# Revit family: 903-20-001-DN65-400
name_source: partatom
category: Pipe Accessories
units: mm (PartAtom-declared; Revit-internal decimal feet)

## family parameters
Always vertical = Yes
Cut with Voids When Loaded = No
Part Type = Valve - Breaks Into
Round Connector Dimension = Use Diameter
Shared = No
Work Plane-Based = No

## types (15) — shared parameters
903-065-20-11000 = DN65_PN16
903-080-20-11000 = DN80_PN16
903-100-20-11000 = DN100_PN16
903-125-20-11000 = DN125_PN16
903-150-20-11000 = DN150_PN16
903-200-20-01000 = DN200_PN10
903-200-20-11000 = DN200_PN16
903-250-20-01000 = DN250_PN10
903-250-20-11000 = DN250_PN16
903-300-20-01000 = DN300_PN10
903-300-20-11000 = DN300_PN16
903-350-20-01000 = DN350_PN10
903-350-20-11000 = DN350_PN16
903-400-20-01000 = DN400_PN10
903-400-20-11000 = DN400_PN16
Description_ = AVK SILENT CHECK VALVE
Search_table = 903-20-001-DN65-400
URL product pages = https://www.avkvalves.com

## per-type parameters (varying)
| type | Bodywall_thickness | D2 | DN | Flange_thickness | Flange_thickness_2 | Flange_thickness_3 | ID | L | L_ref | L_ref_2 | W |
| DN065_PN16 | 43 mm | 59 mm | 65 mm  [stored 0.213255 ft] | 10 mm  [stored 0.0328084 ft] | 5 mm  [stored 0.0164042 ft] | 15 mm  [stored 0.0492126 ft] | 33 mm | 140 mm  [stored 0.459318 ft] | 20 mm  [stored 0.0656168 ft] | 15 mm  [stored 0.0492126 ft] | 93 mm |
| DN080_PN16 | 50 mm  [stored 0.164042 ft] | 66 mm  [stored 0.216535 ft] | 80 mm  [stored 0.262467 ft] | 10 mm  [stored 0.0328084 ft] | 5 mm  [stored 0.0164042 ft] | 15 mm  [stored 0.0492126 ft] | 40 mm  [stored 0.131234 ft] | 152 mm  [stored 0.498688 ft] | 15 mm  [stored 0.0492126 ft] | 20 mm  [stored 0.0656168 ft] | 100 mm  [stored 0.328084 ft] |
| DN100_PN16 | 60 mm  [stored 0.19685 ft] | 78 mm  [stored 0.255906 ft] | 100 mm  [stored 0.328084 ft] | 10 mm  [stored 0.0328084 ft] | 5 mm  [stored 0.0164042 ft] | 15 mm  [stored 0.0492126 ft] | 50 mm  [stored 0.164042 ft] | 184 mm  [stored 0.603675 ft] | 20 mm  [stored 0.0656168 ft] | 20 mm  [stored 0.0656168 ft] | 118 mm  [stored 0.387139 ft] |
| DN125_PN16 | 73 mm | 92 mm  [stored 0.301837 ft] | 125 mm  [stored 0.410105 ft] | 10 mm  [stored 0.0328084 ft] | 5 mm  [stored 0.0164042 ft] | 15 mm  [stored 0.0492126 ft] | 63 mm | 216 mm | 20 mm  [stored 0.0656168 ft] | 25 mm  [stored 0.082021 ft] | 135 mm  [stored 0.442913 ft] |
| DN150_PN16 | 85 mm  [stored 0.278871 ft] | 106 mm | 150 mm  [stored 0.492126 ft] | 10 mm  [stored 0.0328084 ft] | 5 mm  [stored 0.0164042 ft] | 15 mm  [stored 0.0492126 ft] | 75 mm  [stored 0.246063 ft] | 248 mm | 25 mm  [stored 0.082021 ft] | 35 mm  [stored 0.114829 ft] | 150 mm  [stored 0.492126 ft] |
| DN200_PN10 | 110 mm  [stored 0.360892 ft] | 133 mm  [stored 0.436352 ft] | 200 mm | 15 mm  [stored 0.0492126 ft] | 8 mm  [stored 0.0262467 ft] | 23 mm | 100 mm  [stored 0.328084 ft] | 317 mm | 40 mm  [stored 0.131234 ft] | 30 mm  [stored 0.0984252 ft] | 180 mm  [stored 0.590551 ft] |
| DN200_PN16 | 110 mm  [stored 0.360892 ft] | 133 mm  [stored 0.436352 ft] | 200 mm | 15 mm  [stored 0.0492126 ft] | 8 mm  [stored 0.0262467 ft] | 23 mm | 100 mm  [stored 0.328084 ft] | 317 mm | 40 mm  [stored 0.131234 ft] | 30 mm  [stored 0.0984252 ft] | 180 mm  [stored 0.590551 ft] |
| DN250_PN10 | 135 mm  [stored 0.442913 ft] | 160 mm  [stored 0.524934 ft] | 250 mm | 15 mm  [stored 0.0492126 ft] | 8 mm  [stored 0.0262467 ft] | 23 mm | 125 mm  [stored 0.410105 ft] | 394 mm | 55 mm  [stored 0.180446 ft] | 60 mm  [stored 0.19685 ft] | 220 mm |
| DN250_PN16 | 135 mm  [stored 0.442913 ft] | 160 mm  [stored 0.524934 ft] | 250 mm | 15 mm  [stored 0.0492126 ft] | 8 mm  [stored 0.0262467 ft] | 23 mm | 125 mm  [stored 0.410105 ft] | 394 mm | 55 mm  [stored 0.180446 ft] | 60 mm  [stored 0.19685 ft] | 220 mm |
| DN300_PN10 | 160 mm  [stored 0.524934 ft] | 185 mm | 300 mm | 20 mm  [stored 0.0656168 ft] | 10 mm  [stored 0.0328084 ft] | 30 mm  [stored 0.0984252 ft] | 150 mm  [stored 0.492126 ft] | 362 mm | 60 mm  [stored 0.19685 ft] | 40 mm  [stored 0.131234 ft] | 250 mm |
| DN300_PN16 | 160 mm  [stored 0.524934 ft] | 185 mm | 300 mm | 20 mm  [stored 0.0656168 ft] | 10 mm  [stored 0.0328084 ft] | 30 mm  [stored 0.0984252 ft] | 150 mm  [stored 0.492126 ft] | 362 mm | 60 mm  [stored 0.19685 ft] | 40 mm  [stored 0.131234 ft] | 250 mm |
| DN350_PN10 | 185 mm | 215 mm | 350 mm | 20 mm  [stored 0.0656168 ft] | 10 mm  [stored 0.0328084 ft] | 30 mm  [stored 0.0984252 ft] | 175 mm  [stored 0.574147 ft] | 400 mm | 80 mm  [stored 0.262467 ft] | 50 mm  [stored 0.164042 ft] | 290 mm |
| DN350_PN16 | 185 mm | 215 mm | 350 mm | 20 mm  [stored 0.0656168 ft] | 10 mm  [stored 0.0328084 ft] | 30 mm  [stored 0.0984252 ft] | 175 mm  [stored 0.574147 ft] | 400 mm | 80 mm  [stored 0.262467 ft] | 50 mm  [stored 0.164042 ft] | 290 mm |
| DN400_PN10 | 210 mm | 275 mm | 400 mm | 20 mm  [stored 0.0656168 ft] | 10 mm  [stored 0.0328084 ft] | 30 mm  [stored 0.0984252 ft] | 200 mm | 448 mm | 80 mm  [stored 0.262467 ft] | 50 mm  [stored 0.164042 ft] | 318 mm |
| DN400_PN16 | 210 mm | 275 mm | 400 mm | 20 mm  [stored 0.0656168 ft] | 10 mm  [stored 0.0328084 ft] | 30 mm  [stored 0.0984252 ft] | 200 mm | 448 mm | 80 mm  [stored 0.262467 ft] | 50 mm  [stored 0.164042 ft] | 318 mm |

note: [stored X ft] marks values corroborated as IEEE doubles in the binary element streams (Revit-internal decimal feet)

## geometry (parser evidence)
native form markers: Sweep x11
no freeform markers — native parametric forms only
